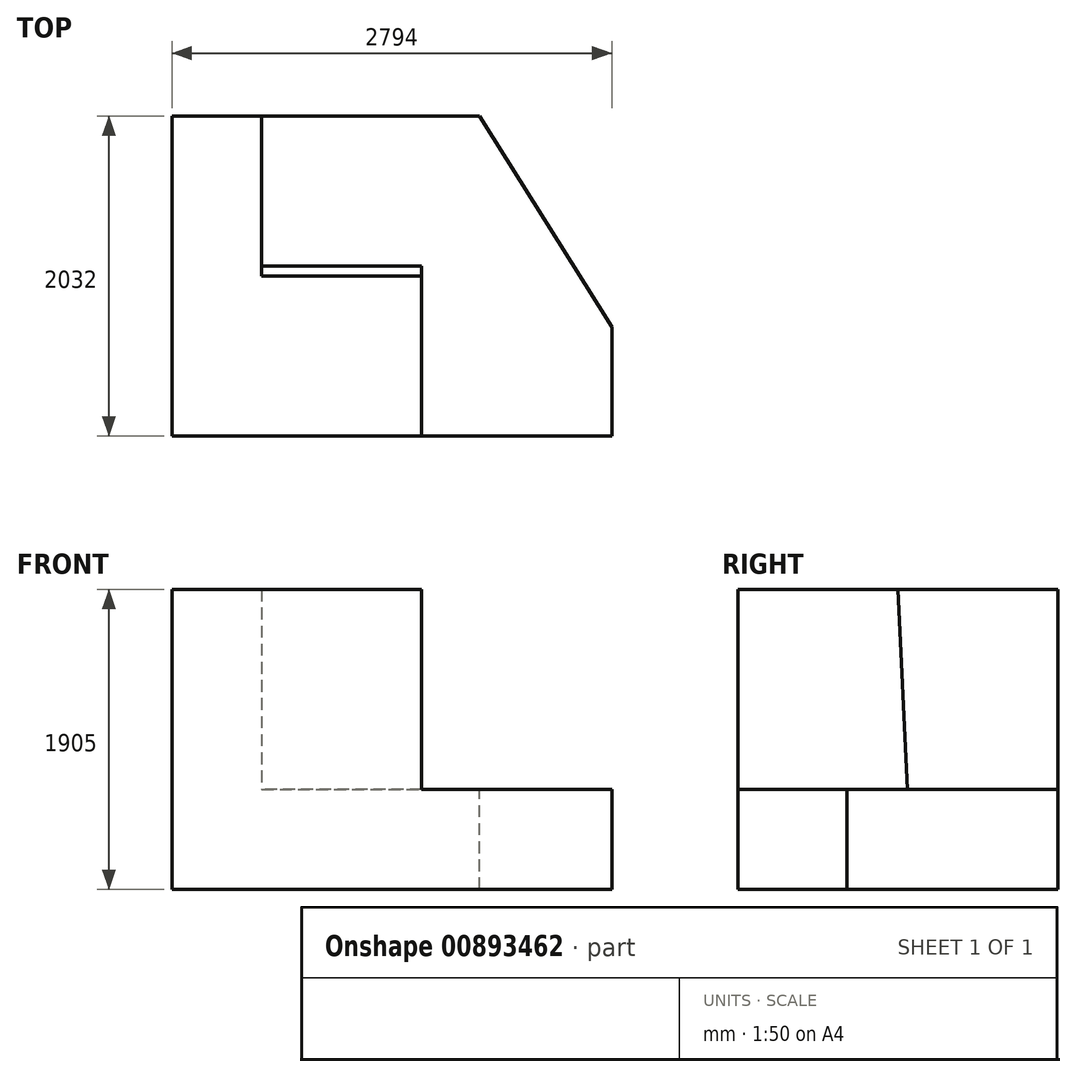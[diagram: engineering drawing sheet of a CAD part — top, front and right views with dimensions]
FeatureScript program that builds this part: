
annotation { "Feature Type Name" : "Feature", "Feature Type Description" : "" }
export const myFeature = defineFeature(function(context is Context, id is Id, definition is map)
    precondition{}
    {
        {
            var Q0;
            Q0=qCreatedBy(makeId("Top.planeOp"),FACE);
            var sketch = newSketch(context, id + "F0", { "sketchPlane" : qUnion([Q0])});
            skLineSegment(sketch, "E0.bottom", {"start": v(-2716.06, 953.83) * mm, "end": v(77.94, 953.83) * mm});
            skLineSegment(sketch, "E0.top", {"start": v(-2716.06, -62.17) * mm, "end": v(77.94, -62.17) * mm});
            skLineSegment(sketch, "E0.left", {"start": v(-2716.06, 953.83) * mm, "end": v(-2716.06, -62.17) * mm});
            skLineSegment(sketch, "E0.right", {"start": v(77.94, 953.83) * mm, "end": v(77.94, -62.17) * mm});
            skLineSegment(sketch, "E1.bottom", {"start": v(-745.5, -873.32) * mm, "end": v(-671.63, -873.32) * mm});
            skLineSegment(sketch, "E1.top", {"start": v(-745.5, -994.82) * mm, "end": v(-671.63, -994.82) * mm});
            skLineSegment(sketch, "E1.left", {"start": v(-745.5, -873.32) * mm, "end": v(-745.5, -994.82) * mm});
            skLineSegment(sketch, "E1.right", {"start": v(-671.63, -873.32) * mm, "end": v(-671.63, -994.82) * mm});
            skSolve(sketch);
        }
        {
            var Q0;
            Q0=makeQuery(id+"F0.imprint","IMPRINT",FACE,{"disambiguationData":[TD([[makeQuery(id+"F0.imprint","IMPRINT",EDGE,{"derivedFrom":sQuery(id+"F0.wireOp",EDGE,"E0.bottom")}),-1.0]])]});
            var sketch = newSketch(context, id + "F1", { "sketchPlane" : qUnion([Q0])});
            skSolve(sketch);
        }
        {
            var Q0;
            Q0 = qSketchRegion(id + "F1", true);
            var Q1;
            Q1=makeQuery(id+"F0.imprint","IMPRINT",FACE,{"disambiguationData":[TD([[makeQuery(id+"F0.imprint","IMPRINT",EDGE,{"derivedFrom":sQuery(id+"F0.wireOp",EDGE,"E0.bottom")}),-1.0]])]});
            extrude(context, id + "F2", {"entities" : qUnion([Q0, Q1]), "depth" : 635 * mm, "offsetDistance" : 25.4 * mm});
        }
        {
            var Q0;
            Q0=makeQuery(id+"F2.opExtrude","CAP_FACE",FACE,{"disambiguationData":[OSD([sQuery(id+"F0.wireOp",EDGE,"E0.bottom"),sQuery(id+"F0.wireOp",EDGE,"E0.top"),sQuery(id+"F0.wireOp",EDGE,"E0.left"),sQuery(id+"F0.wireOp",EDGE,"E0.right")])],"isStart":false});
            var sketch = newSketch(context, id + "F3", { "sketchPlane" : qUnion([Q0])});
            skLineSegment(sketch, "E2", {"start": v(-2145.53, 953.83) * mm, "end": v(-2145.53, -62.17) * mm});
            skSolve(sketch);
        }
        {
            var Q0;
            {var subQ0=sQuery(id+"F3.wireOp",EDGE,"E2");Q0=makeQuery(id+"F3.imprint","IMPRINT",FACE,{"disambiguationData":[TD([[makeQuery(id+"F3.imprint","IMPRINT",EDGE,{"derivedFrom":subQ0}),-1.0]])]});}
            extrude(context, id + "F4", {"entities" : qUnion([Q0]), "operationType" : NewBodyOperationType.ADD, "depth" : 1270 * mm, "offsetDistance" : 25.4 * mm});
        }
        {
            var Q0;
            {var subQ0=sQuery(id+"F0.wireOp",EDGE,"E0.top");Q0=makeQuery(id+"F4.boolean.opBoolean","MERGE",FACE,{"derivedFrom":[makeQuery(id+"F2.opExtrude","SWEPT_FACE",FACE,{"disambiguationData":[OSD([subQ0])]}),makeQuery(id+"F4.opExtrude","SWEPT_FACE",FACE,{"disambiguationData":[OSD([subQ0])]})]});}
            extrude(context, id + "F5", {"entities" : qUnion([Q0]), "operationType" : NewBodyOperationType.ADD, "depth" : 1016 * mm, "offsetDistance" : 25.4 * mm});
        }
        {
            var Q0;
            {var subQ0=sQuery(id+"F3.wireOp",EDGE,"E2");Q0=makeQuery(id+"F5.boolean.opBoolean","MERGE",FACE,{"derivedFrom":[makeQuery(id+"F4.opExtrude","SWEPT_FACE",FACE,{"disambiguationData":[OSD([subQ0])]}),makeQuery(id+"F5.opExtrude","SWEPT_FACE",FACE,{"disambiguationData":[OSD([sQuery(id+"F0.wireOp",EDGE,"E0.top"),subQ0])]})]});}
            var sketch = newSketch(context, id + "F6", { "sketchPlane" : qUnion([Q0])});
            skLineSegment(sketch, "E3", {"start": v(-62.17, 1905) * mm, "end": v(0, 635) * mm});
            skSolve(sketch);
        }
        {
            var Q0;
            {var subQ0=sQuery(id+"F6.wireOp",EDGE,"E3");Q0=makeQuery(id+"F6.imprint","IMPRINT",FACE,{"disambiguationData":[TD([[makeQuery(id+"F6.imprint","IMPRINT",EDGE,{"derivedFrom":subQ0}),-1.0]])]});}
            extrude(context, id + "F7", {"entities" : qUnion([Q0]), "operationType" : NewBodyOperationType.ADD, "depth" : 1016 * mm, "offsetDistance" : 25.4 * mm});
        }
        {
            var Q0;
            {var subQ0=sQuery(id+"F0.wireOp",EDGE,"E0.top");Q0=makeQuery(id+"F5.boolean.opBoolean","MERGE",FACE,{"derivedFrom":[makeQuery(id+"F2.opExtrude","CAP_FACE",FACE,{"disambiguationData":[OSD([sQuery(id+"F0.wireOp",EDGE,"E0.bottom"),subQ0,sQuery(id+"F0.wireOp",EDGE,"E0.left"),sQuery(id+"F0.wireOp",EDGE,"E0.right")])],"isStart":false}),makeQuery(id+"F5.opExtrude","SWEPT_FACE",FACE,{"disambiguationData":[OSD([subQ0]),TDD([makeQuery(id+"F2.opExtrude","CAP_EDGE",EDGE,{"disambiguationData":[OSD([subQ0])],"isStart":false})])]})]});}
            var sketch = newSketch(context, id + "F8", { "sketchPlane" : qUnion([Q0])});
            skLineSegment(sketch, "E4", {"start": v(-762.42, 953.83) * mm, "end": v(77.94, -385.05) * mm});
            skSolve(sketch);
        }
        {
            var Q0;
            {var subQ0=sQuery(id+"F8.wireOp",EDGE,"E4");Q0=makeQuery(id+"F8.imprint","IMPRINT",FACE,{"disambiguationData":[TD([[makeQuery(id+"F8.imprint","IMPRINT",EDGE,{"derivedFrom":subQ0}),1.0]])]});}
            extrude(context, id + "F9", {"entities" : qUnion([Q0]), "operationType" : NewBodyOperationType.REMOVE, "oppositeDirection" : true, "depth" : 2540 * mm, "offsetDistance" : 25.4 * mm});
        }
    });
